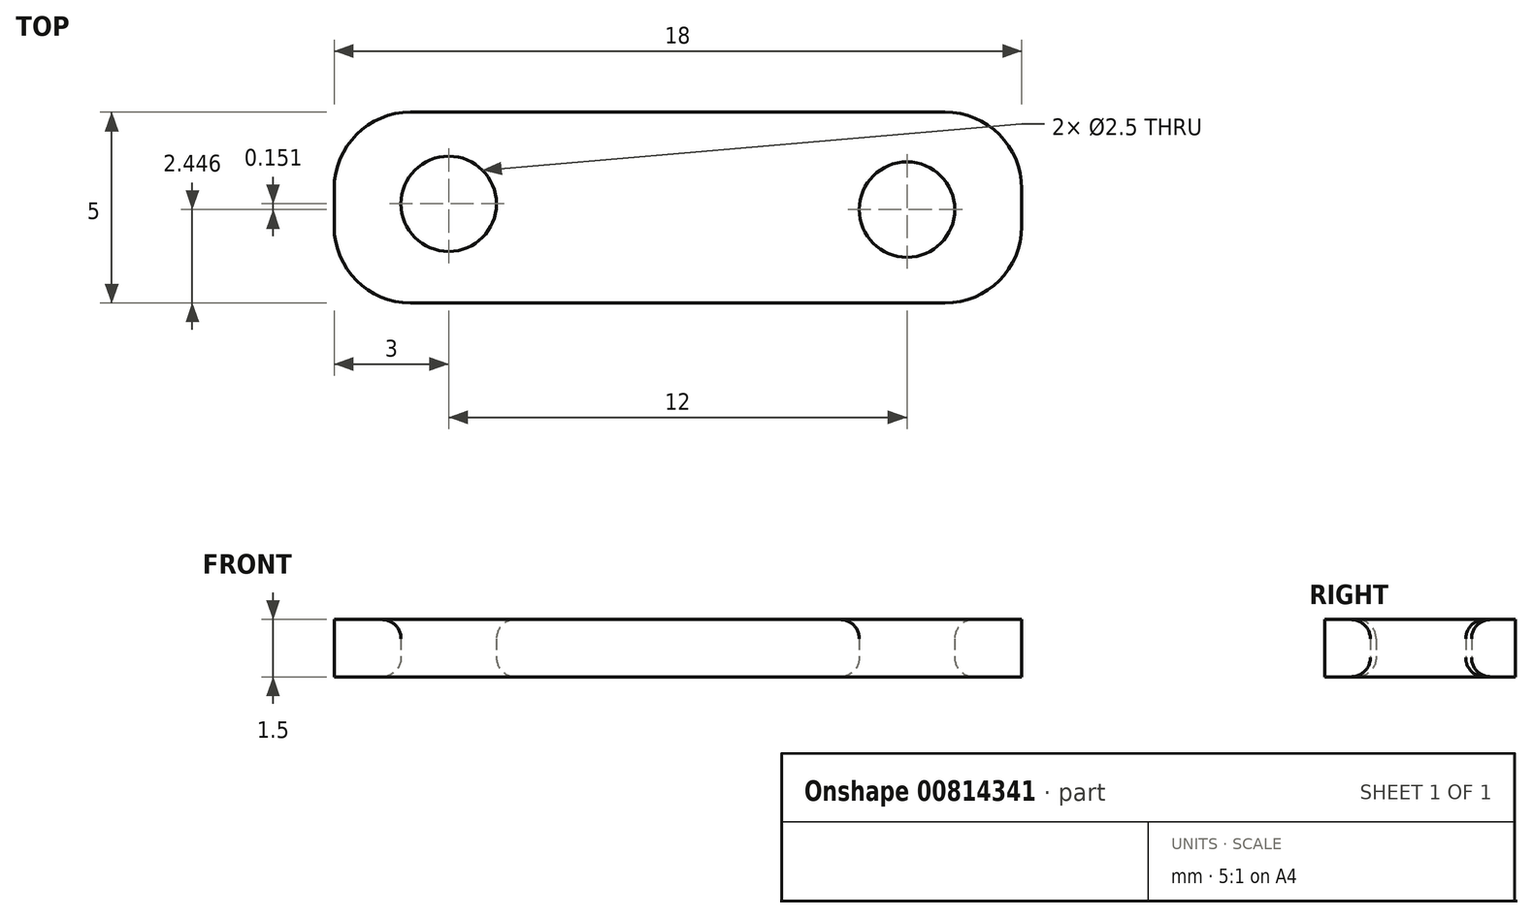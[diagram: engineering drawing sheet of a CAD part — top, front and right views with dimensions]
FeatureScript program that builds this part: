
annotation { "Feature Type Name" : "Feature", "Feature Type Description" : "" }
export const myFeature = defineFeature(function(context is Context, id is Id, definition is map)
    precondition{}
    {
        {
            var Q0;
            Q0=qCreatedBy(makeId("Top.planeOp"),FACE);
            var sketch = newSketch(context, id + "F0", { "sketchPlane" : qUnion([Q0])});
            skLineSegment(sketch, "E0.bottom", {"start": v(0, 0) * mm, "end": v(18, 0) * mm});
            skLineSegment(sketch, "E0.top", {"start": v(0, 5) * mm, "end": v(18, 5) * mm});
            skLineSegment(sketch, "E0.left", {"start": v(0, 0) * mm, "end": v(0, 5) * mm});
            skLineSegment(sketch, "E0.right", {"start": v(18, 0) * mm, "end": v(18, 5) * mm});
            skSolve(sketch);
        }
        {
            var Q0;
            Q0=makeQuery(id+"F0.imprint","IMPRINT",FACE,{"disambiguationData":[TD([[makeQuery(id+"F0.imprint","IMPRINT",EDGE,{"derivedFrom":sQuery(id+"F0.wireOp",EDGE,"E0.bottom")}),1.0]])]});
            var sketch = newSketch(context, id + "F1", { "sketchPlane" : qUnion([Q0])});
            skCircle(sketch, "E1", {"center": v(3, 2.6) * mm, "radius": 1.25 * mm});
            skCircle(sketch, "E2", {"center": v(15, 2.45) * mm, "radius": 1.25 * mm});
            skSolve(sketch);
        }
        {
            var Q0;
            Q0=makeQuery(id+"F1.imprint","IMPRINT",FACE,{"disambiguationData":[TD([[makeQuery(id+"F1.imprint","IMPRINT",EDGE,{"derivedFrom":sQuery(id+"F1.wireOp",EDGE,"E1")}),-1.0]])]});
            extrude(context, id + "F2", {"entities" : qUnion([Q0]), "depth" : 1.5 * mm, "offsetDistance" : 25 * mm});
        }
        {
            var Q0;
            Q0=makeQuery(id+"F2.opExtrude","SWEPT_EDGE",EDGE,{"disambiguationData":[OSD([sQuery(id+"F0.wireOp",EDGE,"E0.top"),sQuery(id+"F0.wireOp",EDGE,"E0.left")])]});
            var Q1;
            Q1=makeQuery(id+"F2.opExtrude","SWEPT_EDGE",EDGE,{"disambiguationData":[OSD([sQuery(id+"F0.wireOp",EDGE,"E0.bottom"),sQuery(id+"F0.wireOp",EDGE,"E0.left")])]});
            var Q2;
            Q2=makeQuery(id+"F2.opExtrude","SWEPT_EDGE",EDGE,{"disambiguationData":[OSD([sQuery(id+"F0.wireOp",EDGE,"E0.bottom"),sQuery(id+"F0.wireOp",EDGE,"E0.right")])]});
            var Q3;
            Q3=makeQuery(id+"F2.opExtrude","SWEPT_EDGE",EDGE,{"disambiguationData":[OSD([sQuery(id+"F0.wireOp",EDGE,"E0.top"),sQuery(id+"F0.wireOp",EDGE,"E0.right")])]});
            fillet(context, id + "F3", {"entities" : qUnion([Q0, Q1, Q2, Q3]), "radius" : 2 * mm, "tangentPropagation" : true, "allowEdgeOverflow" : false});
        }
        {
            var Q0;
            Q0=makeQuery(id+"F2.opExtrude","CAP_EDGE",EDGE,{"disambiguationData":[OSD([sQuery(id+"F1.wireOp",EDGE,"E1")])],"isStart":false});
            var Q1;
            Q1=makeQuery(id+"F2.opExtrude","SWEPT_FACE",FACE,{"disambiguationData":[OSD([sQuery(id+"F1.wireOp",EDGE,"E2")])]});
            var Q2;
            Q2=makeQuery(id+"F2.opExtrude","CAP_EDGE",EDGE,{"disambiguationData":[OSD([sQuery(id+"F1.wireOp",EDGE,"E1")])],"isStart":true});
            fillet(context, id + "F4", {"entities" : qUnion([Q0, Q1, Q2]), "radius" : 0.5 * mm, "tangentPropagation" : true, "allowEdgeOverflow" : false});
        }
    });
